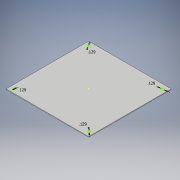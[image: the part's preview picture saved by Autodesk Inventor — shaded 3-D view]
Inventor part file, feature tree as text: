
AUTODESK INVENTOR PART (.ipt)
format: ipt  version: 2018 (Build 220112000, 112)  size: 97,792 bytes
history: native  units: in
note: dims shown in document units (in); Inventor stores cm internally (conversion verified against a paired STEP export)
features: sketch x2, extrude x1
ambient origin geometry x8: Origin, YZ Plane, XZ Plane, XY Plane, X Axis, Y Axis, Z Axis, Center Point
bodies: Solid1 (feature_tree)
feature tree (3):
  extrude  "Extrusion1"  Depth=3.937in
  sketch  "Sketch2"  dims[d2=0.031in d3=0.0in d4=0.1285in d5=0.1285in d6=0.1285in d7=0.1285in]
  sketch  "Sketch1"  dims[d0=3.937in d1=3.937in]
